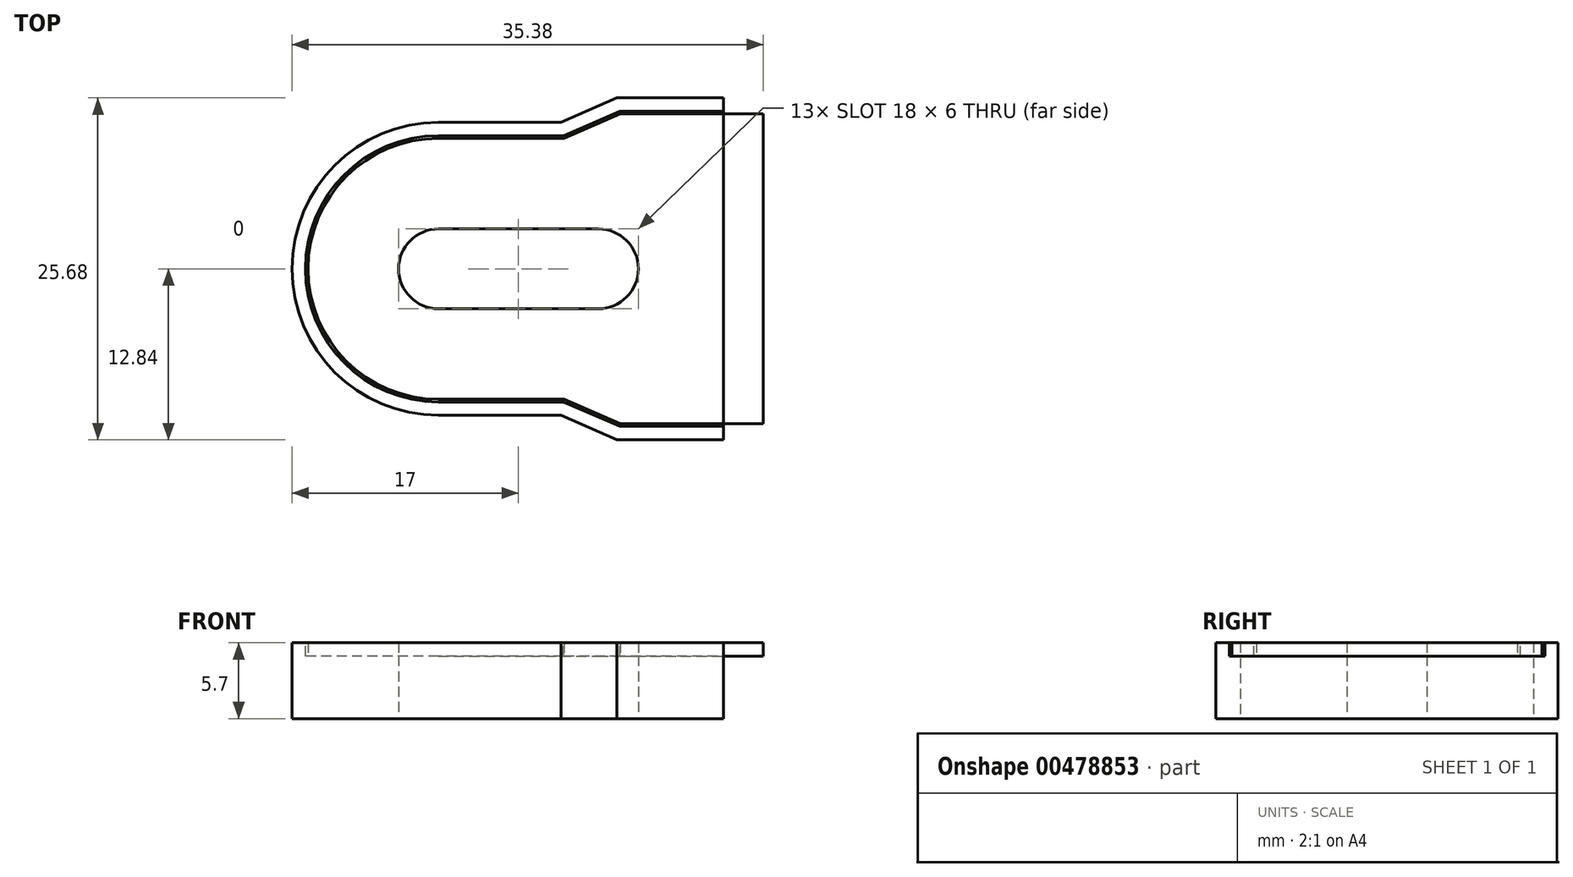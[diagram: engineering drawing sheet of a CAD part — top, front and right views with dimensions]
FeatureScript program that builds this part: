
annotation { "Feature Type Name" : "Feature", "Feature Type Description" : "" }
export const myFeature = defineFeature(function(context is Context, id is Id, definition is map)
    precondition{}
    {
        {
            var Q0;
            Q0=qCreatedBy(makeId("Top.planeOp"),FACE);
            var sketch = newSketch(context, id + "F0", { "sketchPlane" : qUnion([Q0])});
            skLineSegment(sketch, "E0.bottom", {"start": v(-6, 3) * mm, "end": v(6, 3) * mm});
            skLineSegment(sketch, "E0.top", {"start": v(-6, -3) * mm, "end": v(6, -3) * mm});
            skLineSegment(sketch, "E0.left", {"start": v(-6, 3) * mm, "end": v(-6, -3) * mm, "construction": true});
            skLineSegment(sketch, "E0.right", {"start": v(6, 3) * mm, "end": v(6, -3) * mm, "construction": true});
            skPoint(sketch, "E0.middle", {"position": v(0, 0) * mm});
            skArc(sketch, "E1", {"start": v(-6, 3) * mm, "mid": v(-9, 0) * mm, "end": v(-6, -3) * mm});
            skArc(sketch, "E2", {"start": v(6, -3) * mm, "mid": v(9, 0) * mm, "end": v(6, 3) * mm});
            skArc(sketch, "E3.0", {"start": v(-6, 11) * mm, "mid": v(-17, 0) * mm, "end": v(-6, -11) * mm});
            skLineSegment(sketch, "E4", {"start": v(-6, 11) * mm, "end": v(3.18, 11) * mm});
            skLineSegment(sketch, "E5", {"start": v(3.18, 11) * mm, "end": v(7.38, 12.84) * mm});
            skLineSegment(sketch, "E6", {"start": v(7.38, 12.84) * mm, "end": v(15.38, 12.84) * mm});
            skLineSegment(sketch, "E7", {"start": v(0, 0) * mm, "end": v(17.8, 0) * mm, "construction": true});
            skLineSegment(sketch, "E8.MirrorCS", {"start": v(-6, -11) * mm, "end": v(3.18, -11) * mm});
            skLineSegment(sketch, "E9.MirrorCS", {"start": v(3.18, -11) * mm, "end": v(7.38, -12.84) * mm});
            skLineSegment(sketch, "E10.MirrorCS", {"start": v(7.38, -12.84) * mm, "end": v(15.38, -12.84) * mm});
            skLineSegment(sketch, "E11", {"start": v(15.38, -12.84) * mm, "end": v(15.38, 12.84) * mm});
            skSolve(sketch);
        }
        {
            var Q0;
            Q0 = qSketchRegion(id + "F0", true);
            extrude(context, id + "F1", {"entities" : qUnion([Q0]), "depth" : 5.7 * mm});
        }
        {
            var Q0;
            Q0=makeQuery(id+"F1.opExtrude","CAP_FACE",FACE,{"disambiguationData":[OSD([sQuery(id+"F0.wireOp",EDGE,"E0.bottom"),sQuery(id+"F0.wireOp",EDGE,"E0.top"),sQuery(id+"F0.wireOp",EDGE,"E1"),sQuery(id+"F0.wireOp",EDGE,"E2"),sQuery(id+"F0.wireOp",EDGE,"E3.0"),sQuery(id+"F0.wireOp",EDGE,"E4"),sQuery(id+"F0.wireOp",EDGE,"E5"),sQuery(id+"F0.wireOp",EDGE,"E6"),sQuery(id+"F0.wireOp",EDGE,"E8.MirrorCS"),sQuery(id+"F0.wireOp",EDGE,"E9.MirrorCS"),sQuery(id+"F0.wireOp",EDGE,"E10.MirrorCS"),sQuery(id+"F0.wireOp",EDGE,"E11")])],"isStart":false});
            var sketch = newSketch(context, id + "F2", { "sketchPlane" : qUnion([Q0])});
            skLineSegment(sketch, "E12.0", {"start": v(3.39, -10) * mm, "end": v(7.6, -11.84) * mm});
            skLineSegment(sketch, "E12.1", {"start": v(-6, -10) * mm, "end": v(3.39, -10) * mm});
            skLineSegment(sketch, "E12.2", {"start": v(7.6, -11.84) * mm, "end": v(12, -11.84) * mm});
            skArc(sketch, "E12.3", {"start": v(-6, 10) * mm, "mid": v(-16, 0) * mm, "end": v(-6, -10) * mm});
            skLineSegment(sketch, "E12.5", {"start": v(12, 11.84) * mm, "end": v(7.6, 11.84) * mm});
            skLineSegment(sketch, "E12.6", {"start": v(7.6, 11.84) * mm, "end": v(3.39, 10) * mm});
            skLineSegment(sketch, "E12.7", {"start": v(3.39, 10) * mm, "end": v(-6, 10) * mm});
            skLineSegment(sketch, "E13", {"start": v(12, 11.84) * mm, "end": v(15.38, 11.84) * mm});
            skLineSegment(sketch, "E14", {"start": v(12, -11.84) * mm, "end": v(15.38, -11.84) * mm});
            skSolve(sketch);
        }
        {
            var Q0;
            Q0 = qSketchRegion(id + "F2", true);
            var Q1;
            Q1=makeQuery(id+"F2.imprint","IMPRINT",FACE,{"disambiguationData":[TD([[makeQuery(id+"F2.imprint","IMPRINT",EDGE,{"derivedFrom":sQuery(id+"F2.wireOp",EDGE,"E12.0")}),1.0]])]});
            extrude(context, id + "F3", {"entities" : qUnion([Q0, Q1]), "operationType" : NewBodyOperationType.REMOVE, "oppositeDirection" : true, "depth" : 1 * mm});
        }
        {
            var Q0;
            Q0=makeQuery(id+"F3.boolean.opBoolean","COPY",FACE,{"derivedFrom":makeQuery(id+"F3.opExtrude","CAP_FACE",FACE,{"disambiguationData":[OSD([sQuery(id+"F0.wireOp",EDGE,"E0.bottom"),sQuery(id+"F0.wireOp",EDGE,"E0.top"),sQuery(id+"F0.wireOp",EDGE,"E1"),sQuery(id+"F0.wireOp",EDGE,"E2"),sQuery(id+"F0.wireOp",EDGE,"E11"),sQuery(id+"F2.wireOp",EDGE,"E12.0"),sQuery(id+"F2.wireOp",EDGE,"E12.1"),sQuery(id+"F2.wireOp",EDGE,"E12.2"),sQuery(id+"F2.wireOp",EDGE,"E12.3"),sQuery(id+"F2.wireOp",EDGE,"E12.5"),sQuery(id+"F2.wireOp",EDGE,"E12.6"),sQuery(id+"F2.wireOp",EDGE,"E12.7"),sQuery(id+"F2.wireOp",EDGE,"E13"),sQuery(id+"F2.wireOp",EDGE,"E14")])],"isStart":false})});
            var sketch = newSketch(context, id + "F4", { "sketchPlane" : qUnion([Q0])});
            skLineSegment(sketch, "E15.0", {"start": v(18.38, -11.64) * mm, "end": v(18.38, 11.64) * mm});
            skLineSegment(sketch, "E15.1", {"start": v(7.63, -11.64) * mm, "end": v(18.38, -11.64) * mm});
            skLineSegment(sketch, "E15.2", {"start": v(18.38, 11.64) * mm, "end": v(7.63, 11.64) * mm});
            skLineSegment(sketch, "E15.3", {"start": v(3.43, -9.8) * mm, "end": v(7.63, -11.64) * mm});
            skLineSegment(sketch, "E15.4", {"start": v(7.63, 11.64) * mm, "end": v(3.43, 9.8) * mm});
            skLineSegment(sketch, "E15.5", {"start": v(3.43, 9.8) * mm, "end": v(-6, 9.8) * mm});
            skArc(sketch, "E15.6", {"start": v(-6, 9.8) * mm, "mid": v(-15.8, 0) * mm, "end": v(-6, -9.8) * mm});
            skLineSegment(sketch, "E15.7", {"start": v(-6, -9.8) * mm, "end": v(3.43, -9.8) * mm});
            skSolve(sketch);
        }
        {
            var Q0;
            {var subQ0=sQuery(id+"F4.wireOp",EDGE,"E15.0");Q0=makeQuery(id+"F4.imprint","IMPRINT",FACE,{"disambiguationData":[TD([[makeQuery(id+"F4.imprint","IMPRINT",EDGE,{"derivedFrom":subQ0}),1.0]])]});}
            var Q1;
            {var subQ0=sQuery(id+"F4.wireOp",EDGE,"E15.3");Q1=makeQuery(id+"F4.imprint","IMPRINT",FACE,{"disambiguationData":[TD([[makeQuery(id+"F4.imprint","IMPRINT",EDGE,{"derivedFrom":subQ0}),1.0]])]});}
            extrude(context, id + "F5", {"entities" : qUnion([Q0, Q1]), "depth" : 1 * mm});
        }
    });
